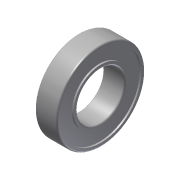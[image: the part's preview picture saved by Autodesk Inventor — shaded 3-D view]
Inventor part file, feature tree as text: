
AUTODESK INVENTOR PART (.ipt)
format: ipt  version: 2013 (Build 170138000, 138)  size: 154,624 bytes
history: native  units: in
note: dims shown in document units (in); Inventor stores cm internally (conversion verified against a paired STEP export)
features: fillet x1, imported_body x1
ambient origin geometry x8: Origin, YZ Plane, XZ Plane, XY Plane, X Axis, Y Axis, Z Axis, Center Point
feature tree (2):
  fillet  "Fillet1"  [1 undecoded]
  imported_body  "Base1"
note: 1 required parameter value undecoded (feature->parameter linkage not recoverable at this tier; creation-order binding heuristic only, values carry confidence <= 0.55)
